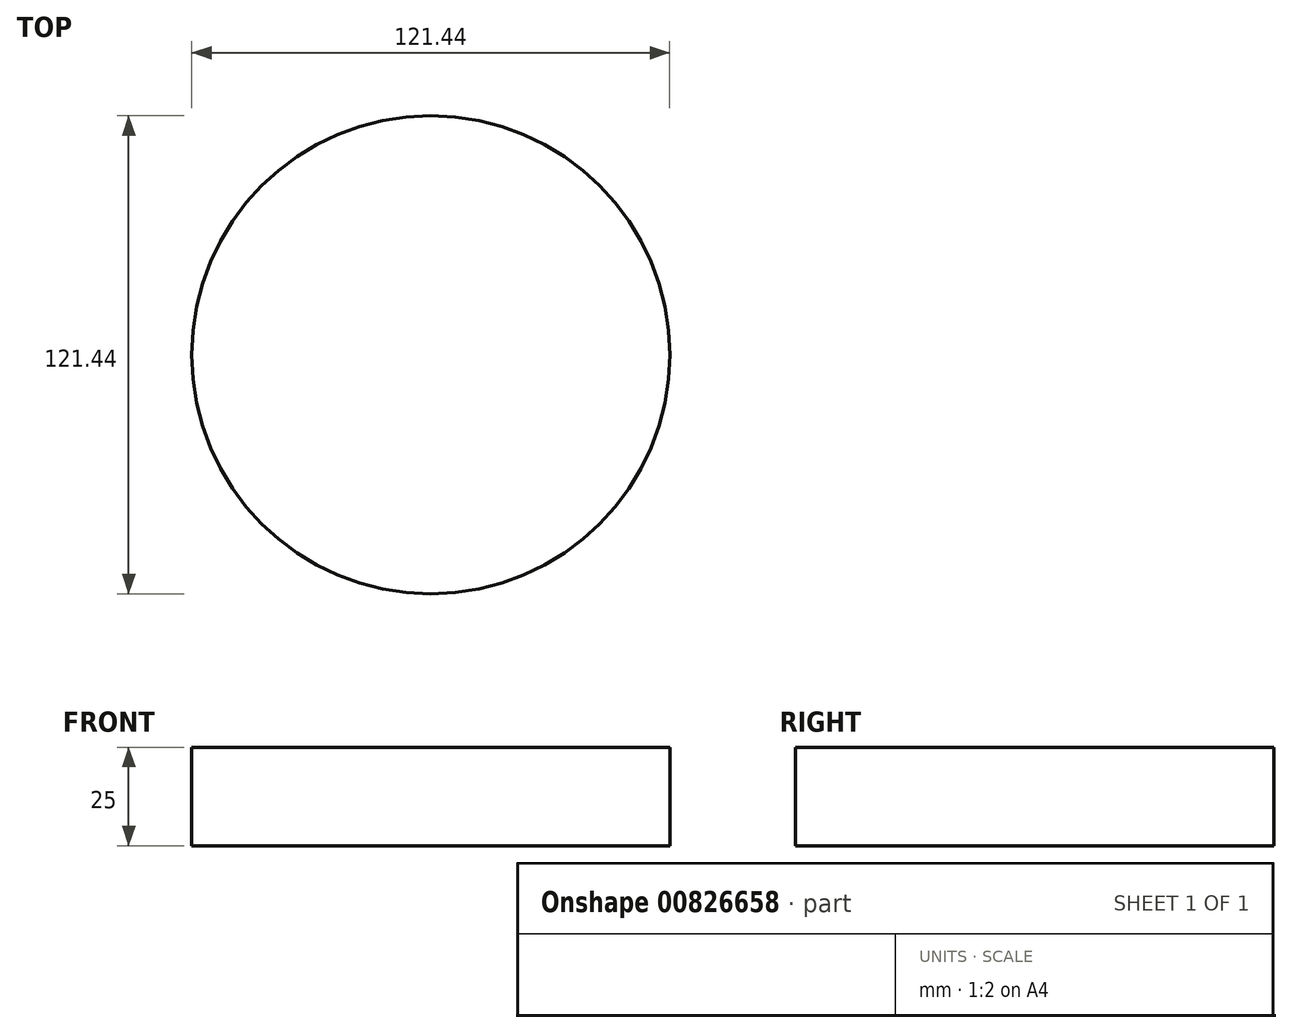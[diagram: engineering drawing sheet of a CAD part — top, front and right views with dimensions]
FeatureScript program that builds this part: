
annotation { "Feature Type Name" : "Feature", "Feature Type Description" : "" }
export const myFeature = defineFeature(function(context is Context, id is Id, definition is map)
    precondition{}
    {
        {
            var Q0;
            Q0=qCreatedBy(makeId("Top.planeOp"),FACE);
            var sketch = newSketch(context, id + "F0", { "sketchPlane" : qUnion([Q0])});
            skCircle(sketch, "E0", {"center": v(0, 0) * mm, "radius": 60.72 * mm});
            skSolve(sketch);
        }
        {
            var Q0;
            Q0=makeQuery(id+"F0.imprint","IMPRINT",FACE,{"disambiguationData":[TD([[makeQuery(id+"F0.imprint","IMPRINT",EDGE,{"derivedFrom":sQuery(id+"F0.wireOp",EDGE,"E0")}),1.0]])]});
            extrude(context, id + "F1", {"entities" : qUnion([Q0]), "depth" : 25 * mm, "offsetDistance" : 25 * mm});
        }
    });
